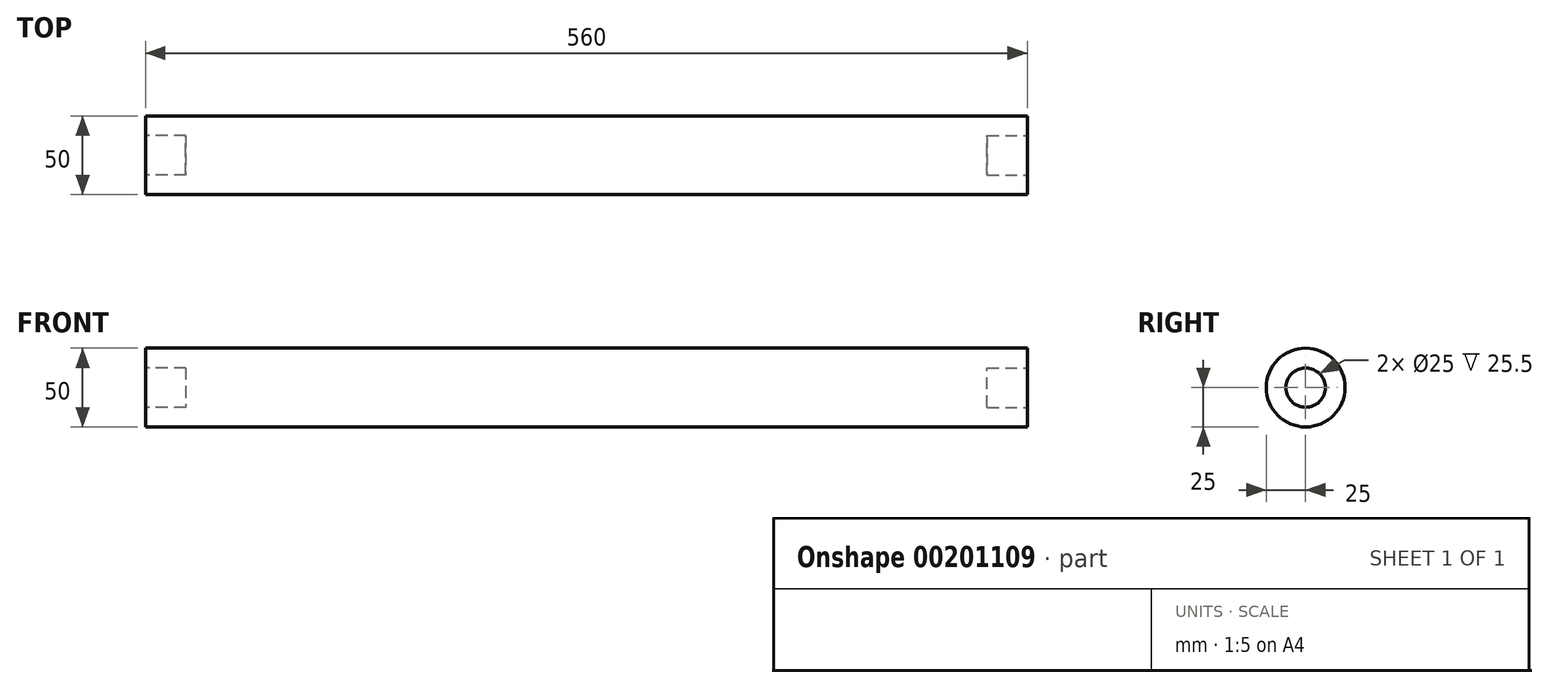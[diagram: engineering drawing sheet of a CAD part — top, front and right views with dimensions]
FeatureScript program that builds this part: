
annotation { "Feature Type Name" : "Feature", "Feature Type Description" : "" }
export const myFeature = defineFeature(function(context is Context, id is Id, definition is map)
    precondition{}
    {
        {
            var Q0;
            Q0=qCreatedBy(makeId("Right.planeOp"),FACE);
            var sketch = newSketch(context, id + "F0", { "sketchPlane" : qUnion([Q0])});
            skCircle(sketch, "E0", {"center": v(0, 0) * mm, "radius": 25 * mm});
            skSolve(sketch);
        }
        {
            var Q0;
            Q0=makeQuery(id+"F0.imprint","IMPRINT",FACE,{"disambiguationData":[TD([[makeQuery(id+"F0.imprint","IMPRINT",EDGE,{"derivedFrom":sQuery(id+"F0.wireOp",EDGE,"E0")}),1.0]])]});
            extrude(context, id + "F1", {"entities" : qUnion([Q0]), "depth" : 560 * mm});
        }
        {
            var Q0;
            Q0=makeQuery(id+"F1.opExtrude","CAP_FACE",FACE,{"disambiguationData":[OSD([sQuery(id+"F0.wireOp",EDGE,"E0")])],"isStart":false});
            var sketch = newSketch(context, id + "F2", { "sketchPlane" : qUnion([Q0])});
            skCircle(sketch, "E1", {"center": v(0, 0) * mm, "radius": 12.5 * mm});
            skSolve(sketch);
        }
        {
            var Q0;
            Q0 = qSketchRegion(id + "F2", true);
            extrude(context, id + "F3", {"entities" : qUnion([Q0]), "operationType" : NewBodyOperationType.REMOVE, "oppositeDirection" : true, "depth" : 25.5 * mm});
        }
        {
            var Q0;
            Q0=makeQuery(id+"F1.opExtrude","CAP_FACE",FACE,{"disambiguationData":[OSD([sQuery(id+"F0.wireOp",EDGE,"E0")])],"isStart":true});
            var sketch = newSketch(context, id + "F4", { "sketchPlane" : qUnion([Q0])});
            skCircle(sketch, "E2", {"center": v(0, 0) * mm, "radius": 12.5 * mm});
            skSolve(sketch);
        }
        {
            var Q0;
            Q0 = qSketchRegion(id + "F4", true);
            extrude(context, id + "F5", {"entities" : qUnion([Q0]), "operationType" : NewBodyOperationType.REMOVE, "oppositeDirection" : true, "depth" : 25.5 * mm});
        }
    });
